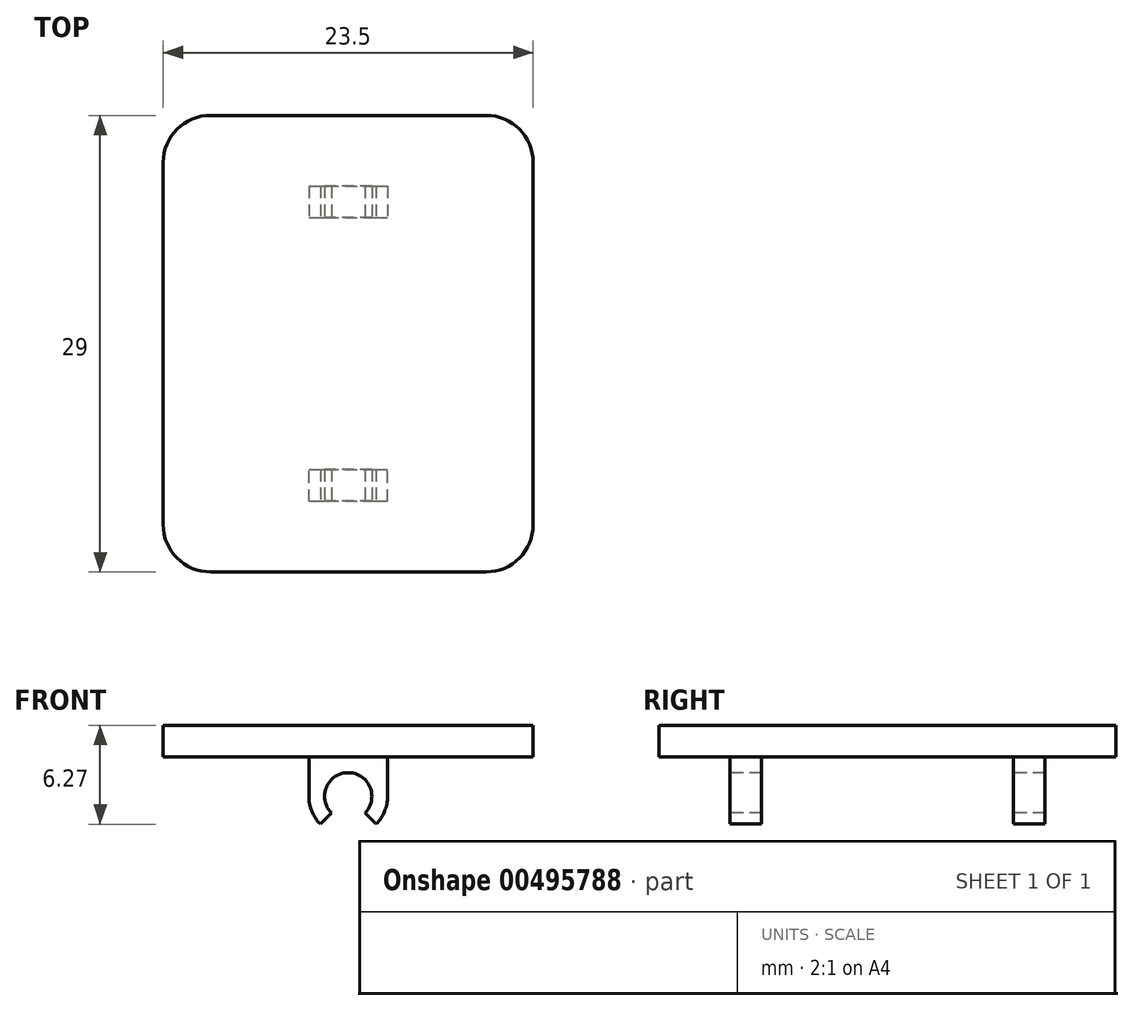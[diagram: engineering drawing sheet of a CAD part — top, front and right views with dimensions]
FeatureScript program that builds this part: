
annotation { "Feature Type Name" : "Feature", "Feature Type Description" : "" }
export const myFeature = defineFeature(function(context is Context, id is Id, definition is map)
    precondition{}
    {
        {
            var Q0;
            Q0=qCreatedBy(makeId("Top.planeOp"),FACE);
            var sketch = newSketch(context, id + "F0", { "sketchPlane" : qUnion([Q0])});
            skPoint(sketch, "E0.middle", {"position": v(0, 0) * mm});
            skLineSegment(sketch, "E1.bottom", {"start": v(8.75, -14.5) * mm, "end": v(-8.75, -14.5) * mm});
            skLineSegment(sketch, "E1.top", {"start": v(8.75, 14.5) * mm, "end": v(-8.75, 14.5) * mm});
            skLineSegment(sketch, "E1.left", {"start": v(11.75, -11.5) * mm, "end": v(11.75, 11.5) * mm});
            skLineSegment(sketch, "E1.right", {"start": v(-11.75, -11.5) * mm, "end": v(-11.75, 11.5) * mm});
            skPoint(sketch, "E2.visualSharp", {"position": v(-11.75, 14.5) * mm});
            skArc(sketch, "E2.filletArc", {"start": v(-8.75, 14.5) * mm, "mid": v(-10.87, 13.62) * mm, "end": v(-11.75, 11.5) * mm});
            skPoint(sketch, "E3.visualSharp", {"position": v(11.75, 14.5) * mm});
            skArc(sketch, "E3.filletArc", {"start": v(11.75, 11.5) * mm, "mid": v(10.87, 13.62) * mm, "end": v(8.75, 14.5) * mm});
            skPoint(sketch, "E4.visualSharp", {"position": v(11.75, -14.5) * mm});
            skArc(sketch, "E4.filletArc", {"start": v(8.75, -14.5) * mm, "mid": v(10.87, -13.62) * mm, "end": v(11.75, -11.5) * mm});
            skPoint(sketch, "E5.visualSharp", {"position": v(-11.75, -14.5) * mm});
            skArc(sketch, "E5.filletArc", {"start": v(-11.75, -11.5) * mm, "mid": v(-10.87, -13.62) * mm, "end": v(-8.75, -14.5) * mm});
            skSolve(sketch);
        }
        {
            var Q0;
            Q0 = qSketchRegion(id + "F0", true);
            extrude(context, id + "F1", {"entities" : qUnion([Q0]), "depth" : 2 * mm});
        }
        {
            var Q0;
            Q0=makeQuery(id+"F1.opExtrude","CAP_FACE",FACE,{"disambiguationData":[OSD([sQuery(id+"F0.wireOp",EDGE,"E1.bottom"),sQuery(id+"F0.wireOp",EDGE,"E1.top"),sQuery(id+"F0.wireOp",EDGE,"E1.left"),sQuery(id+"F0.wireOp",EDGE,"E1.right"),sQuery(id+"F0.wireOp",EDGE,"E2.filletArc"),sQuery(id+"F0.wireOp",EDGE,"E3.filletArc"),sQuery(id+"F0.wireOp",EDGE,"E4.filletArc"),sQuery(id+"F0.wireOp",EDGE,"E5.filletArc")])],"isStart":true});
            var sketch = newSketch(context, id + "F2", { "sketchPlane" : qUnion([Q0])});
            skLineSegment(sketch, "E6.bottom", {"start": v(-2.5, 10) * mm, "end": v(2.5, 10) * mm, "construction": true});
            skLineSegment(sketch, "E6.top", {"start": v(-2.5, -10) * mm, "end": v(2.5, -10) * mm, "construction": true});
            skLineSegment(sketch, "E6.left", {"start": v(-2.5, 10) * mm, "end": v(-2.5, -10) * mm, "construction": true});
            skLineSegment(sketch, "E6.right", {"start": v(2.5, 10) * mm, "end": v(2.5, -10) * mm, "construction": true});
            skPoint(sketch, "E6.middle", {"position": v(0, 0) * mm});
            skLineSegment(sketch, "E7.bottom", {"start": v(-2.5, 10) * mm, "end": v(2.5, 10) * mm});
            skLineSegment(sketch, "E7.top", {"start": v(-2.5, 8) * mm, "end": v(2.5, 8) * mm});
            skLineSegment(sketch, "E7.left", {"start": v(-2.5, 10) * mm, "end": v(-2.5, 8) * mm});
            skLineSegment(sketch, "E7.right", {"start": v(2.5, 10) * mm, "end": v(2.5, 8) * mm});
            skLineSegment(sketch, "E8.bottom", {"start": v(-2.5, -10) * mm, "end": v(2.5, -10) * mm});
            skLineSegment(sketch, "E8.top", {"start": v(-2.5, -8) * mm, "end": v(2.5, -8) * mm});
            skLineSegment(sketch, "E8.left", {"start": v(-2.5, -10) * mm, "end": v(-2.5, -8) * mm});
            skLineSegment(sketch, "E8.right", {"start": v(2.5, -10) * mm, "end": v(2.5, -8) * mm});
            skSolve(sketch);
        }
        {
            var Q0;
            Q0 = qSketchRegion(id + "F2", true);
            extrude(context, id + "F3", {"entities" : qUnion([Q0]), "operationType" : NewBodyOperationType.ADD, "depth" : 5 * mm});
        }
        {
            var Q0;
            Q0=makeQuery(id+"F3.opExtrude","SWEPT_FACE",FACE,{"disambiguationData":[OSD([sQuery(id+"F2.wireOp",EDGE,"E7.bottom")])]});
            var sketch = newSketch(context, id + "F4", { "sketchPlane" : qUnion([Q0])});
            skLineSegment(sketch, "E9", {"start": v(-1.77, -4.27) * mm, "end": v(-1.06, -3.56) * mm, "construction": true});
            skLineSegment(sketch, "E10", {"start": v(1.77, -4.27) * mm, "end": v(1.06, -3.56) * mm, "construction": true});
            skArc(sketch, "E11", {"start": v(1.77, -4.27) * mm, "mid": v(2.3, -3.46) * mm, "end": v(2.5, -2.5) * mm});
            skArc(sketch, "E12", {"start": v(1.06, -3.56) * mm, "mid": v(0, -1) * mm, "end": v(-1.06, -3.56) * mm});
            skLineSegment(sketch, "E13", {"start": v(-1.77, -4.27) * mm, "end": v(-1.06, -3.56) * mm});
            skLineSegment(sketch, "E14", {"start": v(1.06, -3.56) * mm, "end": v(1.77, -4.27) * mm});
            skPoint(sketch, "E15.orphan", {"position": v(2.5, -5) * mm});
            skArc(sketch, "E16.trimOffspring", {"start": v(-2.5, -2.5) * mm, "mid": v(-2.3, -3.46) * mm, "end": v(-1.77, -4.27) * mm});
            skLineSegment(sketch, "E17", {"start": v(-2.5, -2.5) * mm, "end": v(-3.53, -2.82) * mm});
            skLineSegment(sketch, "E18", {"start": v(-3.53, -2.82) * mm, "end": v(-4.29, -6.5) * mm});
            skLineSegment(sketch, "E19", {"start": v(-4.29, -6.5) * mm, "end": v(2.4, -5.65) * mm});
            skLineSegment(sketch, "E20", {"start": v(2.4, -5.65) * mm, "end": v(4, -4.42) * mm});
            skLineSegment(sketch, "E21", {"start": v(4, -4.42) * mm, "end": v(3.52, -2.85) * mm});
            skLineSegment(sketch, "E22", {"start": v(3.52, -2.85) * mm, "end": v(2.5, -2.5) * mm});
            skSolve(sketch);
        }
        {
            var Q0;
            {var subQ4=sQuery(id+"F4.wireOp",EDGE,"E11");Q0=makeQuery(id+"F4.imprint","IMPRINT",FACE,{"disambiguationData":[TD([[makeQuery(id+"F4.imprint","IMPRINT",EDGE,{"derivedFrom":subQ4}),-1.0]])]});}
            var Q1;
            {var subQ0=sQuery(id+"F4.wireOp",EDGE,"E17");Q1=makeQuery(id+"F4.imprint","IMPRINT",FACE,{"disambiguationData":[TD([[makeQuery(id+"F4.imprint","IMPRINT",EDGE,{"derivedFrom":subQ0}),1.0]])]});}
            extrude(context, id + "F5", {"entities" : qUnion([Q0, Q1]), "operationType" : NewBodyOperationType.REMOVE, "oppositeDirection" : true, "depth" : 25 * mm});
        }
    });
